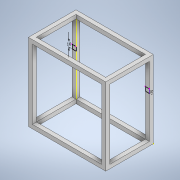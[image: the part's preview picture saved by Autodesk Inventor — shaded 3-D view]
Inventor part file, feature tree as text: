
AUTODESK INVENTOR PART (.ipt)
format: ipt  version: 2020 (Build 240168000, 168)  size: 235,008 bytes
history: native  units: in
note: dims shown in document units (in); Inventor stores cm internally (conversion verified against a paired STEP export)
features: sketch x15, extrude x12
ambient origin geometry x8: Origin, YZ Plane, XZ Plane, XY Plane, X Axis, Y Axis, Z Axis, Center Point
bodies: Solid1 (feature_tree)
feature tree (27):
  extrude  "Extrusion1"  Depth=6.8898in
  extrude  "Extrusion2"  Depth=0.3937in
  extrude  "Extrusion3"  Depth=0.3937in
  extrude  "Extrusion4"  Depth=0.3937in TaperAngle=0.0deg
  extrude  "Extrusion5"  Depth=0.7874in
  sketch  "Sketch6"  dims[d13=3.937in d14=0.0in d15=0.3937in]
  extrude  "Extrusion6"  Depth=0.3937in
  extrude  "Extrusion7"  Depth=0.3937in
  extrude  "Extrusion8"  Depth=3.937in TaperAngle=0.0deg
  extrude  "Extrusion9"  Depth=0.3937in
  extrude  "Extrusion10"  Depth=0.3937in TaperAngle=0.0deg
  extrude  "Extrusion11"  Depth=0.3937in
  extrude  "Extrusion12"  Depth=0.3937in
  sketch  "Sketch15"  dims[d33=35.4331in d34=0.0in]
  sketch  "Sketch16"  dims[d35=0.7874in d36=0.0in d37=0.3937in d38=35.4331in d39=0.0in d40=35.4331in d41=0.0in d45=0.3937in d46=0.3937in]
  sketch  "Sketch1"  dims[d0=6.8898in d1=6.8898in]
  sketch  "Sketch2"  dims[d2=3.937in d3=0.0in d4=0.3937in]
  sketch  "Sketch3"  dims[d5=0.3937in d6=0.3937in]
  sketch  "Sketch4"  dims[d7=0.3937in d8=0.3937in d9=0.0in]
  sketch  "Sketch5"  dims[d10=354.3307in d11=0.0in d12=0.7874in]
  sketch  "Sketch7"  dims[d16=0.3937in d17=0.3937in]
  sketch  "Sketch8"  dims[d18=0.3937in d19=3.937in d20=0.0in]
  sketch  "Sketch9"  dims[d21=0.3937in d22=0.0in d23=0.3937in]
  sketch  "Sketch10"  dims[d24=0.3937in d25=35.4331in d26=0.0in]
  sketch  "Sketch11"  dims[d27=0.3937in d28=0.3937in]
  sketch  "Sketch12"  dims[d29=0.3937in d30=0.3937in]
  sketch  "Sketch13"  dims[d31=35.4331in d32=0.0in]
